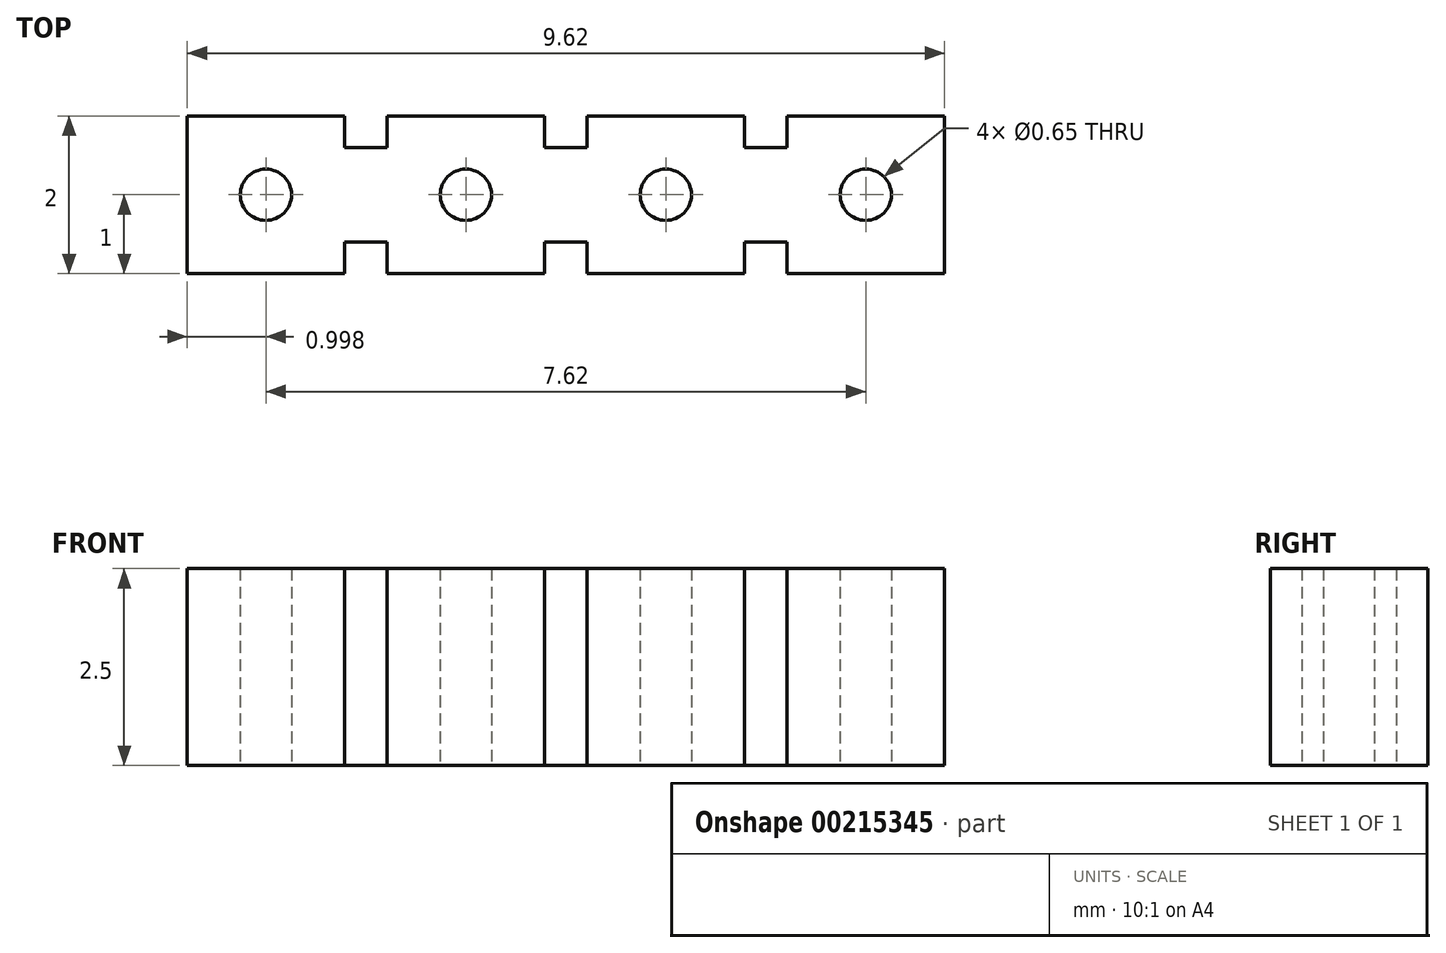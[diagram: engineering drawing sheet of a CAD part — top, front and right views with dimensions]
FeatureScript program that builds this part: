
annotation { "Feature Type Name" : "Feature", "Feature Type Description" : "" }
export const myFeature = defineFeature(function(context is Context, id is Id, definition is map)
    precondition{}
    {
        {
            var Q0;
            Q0=qCreatedBy(makeId("Top.planeOp"),FACE);
            var sketch = newSketch(context, id + "F0", { "sketchPlane" : qUnion([Q0])});
            skLineSegment(sketch, "E0.bottom", {"start": v(-69.27, 0) * mm, "end": v(-71.27, 0) * mm});
            skLineSegment(sketch, "E0.top", {"start": v(-69.27, 2) * mm, "end": v(-71.27, 2) * mm});
            skLineSegment(sketch, "E0.left", {"start": v(-69.27, 0) * mm, "end": v(-69.27, 2) * mm});
            skLineSegment(sketch, "E0.right", {"start": v(-71.27, 0) * mm, "end": v(-71.27, 2) * mm});
            skPoint(sketch, "E0.middle", {"position": v(-70.27, 1) * mm});
            skLineSegment(sketch, "E1.bottom", {"start": v(-69.27, 0.4) * mm, "end": v(-68.73, 0.4) * mm});
            skLineSegment(sketch, "E1.top", {"start": v(-69.27, 1.6) * mm, "end": v(-68.73, 1.6) * mm});
            skLineSegment(sketch, "E1.left", {"start": v(-69.27, 0.4) * mm, "end": v(-69.27, 1.6) * mm});
            skLineSegment(sketch, "E1.right", {"start": v(-68.73, 0.4) * mm, "end": v(-68.73, 1.6) * mm});
            skCircle(sketch, "E2", {"center": v(-70.27, 1) * mm, "radius": 0.33 * mm});
            skLineSegment(sketch, "E3.1.0.0", {"start": v(-66.73, 0.4) * mm, "end": v(-66.73, 1.6) * mm});
            skLineSegment(sketch, "E3.1.0.1", {"start": v(-66.73, 2) * mm, "end": v(-68.73, 2) * mm});
            skLineSegment(sketch, "E3.1.0.2", {"start": v(-66.2, 0.4) * mm, "end": v(-66.2, 1.6) * mm});
            skPoint(sketch, "E3.1.0.3", {"position": v(-67.73, 1) * mm});
            skLineSegment(sketch, "E3.1.0.4", {"start": v(-68.73, 0) * mm, "end": v(-68.73, 2) * mm});
            skCircle(sketch, "E3.1.0.5", {"center": v(-67.73, 1) * mm, "radius": 0.33 * mm});
            skLineSegment(sketch, "E3.1.0.6", {"start": v(-66.73, 0) * mm, "end": v(-66.73, 2) * mm});
            skLineSegment(sketch, "E3.1.0.7", {"start": v(-66.73, 0) * mm, "end": v(-68.73, 0) * mm});
            skLineSegment(sketch, "E3.1.0.8", {"start": v(-66.73, 1.6) * mm, "end": v(-66.2, 1.6) * mm});
            skLineSegment(sketch, "E3.1.0.9", {"start": v(-66.73, 0.4) * mm, "end": v(-66.2, 0.4) * mm});
            skLineSegment(sketch, "E3.2.0.0", {"start": v(-64.2, 0.4) * mm, "end": v(-64.2, 1.6) * mm});
            skLineSegment(sketch, "E3.2.0.1", {"start": v(-64.2, 2) * mm, "end": v(-66.2, 2) * mm});
            skLineSegment(sketch, "E3.2.0.2", {"start": v(-63.65, 0.4) * mm, "end": v(-63.65, 1.6) * mm});
            skPoint(sketch, "E3.2.0.3", {"position": v(-65.2, 1) * mm});
            skLineSegment(sketch, "E3.2.0.4", {"start": v(-66.2, 0) * mm, "end": v(-66.2, 2) * mm});
            skCircle(sketch, "E3.2.0.5", {"center": v(-65.2, 1) * mm, "radius": 0.33 * mm});
            skLineSegment(sketch, "E3.2.0.6", {"start": v(-64.2, 0) * mm, "end": v(-64.2, 2) * mm});
            skLineSegment(sketch, "E3.2.0.7", {"start": v(-64.2, 0) * mm, "end": v(-66.2, 0) * mm});
            skLineSegment(sketch, "E3.2.0.8", {"start": v(-64.2, 1.6) * mm, "end": v(-63.65, 1.6) * mm});
            skLineSegment(sketch, "E3.2.0.9", {"start": v(-64.2, 0.4) * mm, "end": v(-63.65, 0.4) * mm});
            skLineSegment(sketch, "E3.3.0.0", {"start": v(-61.65, 0.4) * mm, "end": v(-61.65, 1.6) * mm});
            skLineSegment(sketch, "E3.3.0.1", {"start": v(-61.65, 2) * mm, "end": v(-63.65, 2) * mm});
            skPoint(sketch, "E3.3.0.3", {"position": v(-62.65, 1) * mm});
            skLineSegment(sketch, "E3.3.0.4", {"start": v(-63.65, 0) * mm, "end": v(-63.65, 2) * mm});
            skCircle(sketch, "E3.3.0.5", {"center": v(-62.65, 1) * mm, "radius": 0.33 * mm});
            skLineSegment(sketch, "E3.3.0.6", {"start": v(-61.65, 0) * mm, "end": v(-61.65, 2) * mm});
            skLineSegment(sketch, "E3.3.0.7", {"start": v(-61.65, 0) * mm, "end": v(-63.65, 0) * mm});
            skLineSegment(sketch, "E3.direction1", {"start": v(-71.27, 0) * mm, "end": v(-68.73, 0) * mm, "construction": true});
            skSolve(sketch);
        }
        {
            var Q0;
            Q0=qSketchRegion(id+"F0",true);
            extrude(context, id + "F1", {"entities" : qUnion([Q0]), "depth" : 2.5 * mm});
        }
    });
